# Revit family: Power-ModularDevices-GEWISS-90AM-SPD_TYPE2_3PN
name_source: partatom
category: Apparecchi elettrici
revit_build: Autodesk Revit 2016 (Build: 20161004_0715(x64)
units: mm (PartAtom-declared; Revit-internal decimal feet)

## family parameters
Condiviso = No
Host = Superficie
Mantenere orientamento annotazione = Sì
Numero OmniClass = 23.80.50.00
Punto di calcolo locali = Sì
Quota connettore circolare = Usa diametro
Taglio con vuoti quando caricato = No
Tipo di parte = Normale
Titolo OmniClass = Terminals for Power Supply

## types (3) — shared parameters
Catalogue = POWER
Catalogue Range = 90 AM
Electrocod = 0642
IDF = 0c95a6d0-63f0-4ff1-9e15-2ee034f6c6a2
IDT = 85bb85a7-02e4-43ec-b182-c73c4bf8262c
Immagine tipo = GWD6420.jpg
No. Chorus modules = 4
No. of modules EN 50022 = 4
No. of poles = 3P+N
Number of poles = 3P+N
Numero di poli = 1
Produttore = GEWISS S.p.A.
Prospetto di default = 1219 mm
Rated voltage = 400Vac
Rated voltage AC = 400V
SEO = Limiter
Spostamento_x = -340 mm
Technical sheet = https://www.gewiss.com
Type = 2
Type: = 2
URL = https://www.gewiss.com
Version file RFA = 18.0
carico = Altro
potenza in watt = 0 V

## per-type parameters (varying)
| type | Descrizione | EAN code | Maximum discharge current: | Modello |
| GWD6420 - LST - SPD 3P+N 40KA AUX. T2 | LST - SPD 3P+N 40KA AUX. T2 | 8011564775022 | 40KA | GWD6420 |
| GWD6409 - LST - SPD 3P+N 20KA T2 | LST - SPD 3P+N 20KA T2 | 8011564774858 | 20KA | GWD6409 |
| GWD6419 - LST - SPD 3P+N 40KA T2 | LST - SPD 3P+N 40KA T2 | 8011564775015 | 40KA | GWD6419 |
